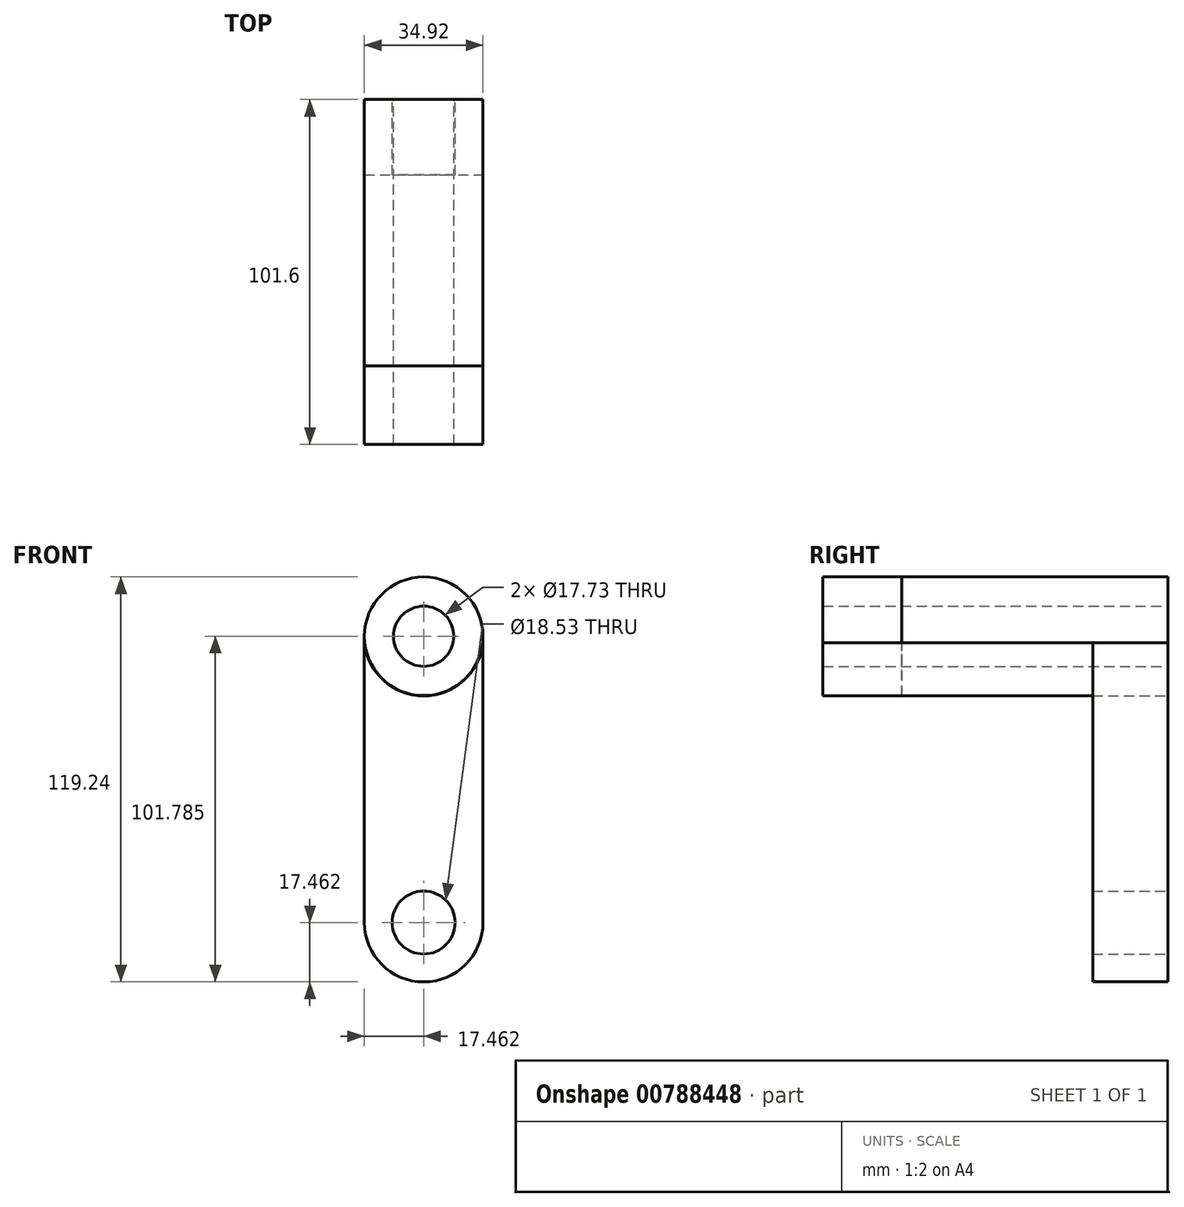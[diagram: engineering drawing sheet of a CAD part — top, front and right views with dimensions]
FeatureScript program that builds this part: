
annotation { "Feature Type Name" : "Feature", "Feature Type Description" : "" }
export const myFeature = defineFeature(function(context is Context, id is Id, definition is map)
    precondition{}
    {
        {
            var Q0;
            Q0=qCreatedBy(makeId("Front.planeOp"),FACE);
            var sketch = newSketch(context, id + "F0", { "sketchPlane" : qUnion([Q0])});
            skLineSegment(sketch, "E0.left", {"start": v(-20.9, 24.35) * mm, "end": v(-20.9, -59.97) * mm});
            skLineSegment(sketch, "E0.right", {"start": v(14, 24.35) * mm, "end": v(14, -59.97) * mm});
            skArc(sketch, "E1", {"start": v(14, 24.35) * mm, "mid": v(-3.45, 41.81) * mm, "end": v(-20.9, 24.35) * mm});
            skArc(sketch, "E2", {"start": v(-20.9, -59.97) * mm, "mid": v(-3.45, -77.43) * mm, "end": v(14, -59.97) * mm});
            skCircle(sketch, "E3", {"center": v(-3.45, 24.35) * mm, "radius": 8.86 * mm});
            skCircle(sketch, "E4", {"center": v(-3.45, -59.97) * mm, "radius": 9.27 * mm});
            skCircle(sketch, "E5", {"center": v(-3.45, 24.35) * mm, "radius": 17.57 * mm});
            skSolve(sketch);
        }
        {
            var Q0;
            Q0=makeQuery(id+"F0.imprint","IMPRINT",FACE,{"disambiguationData":[TD([[makeQuery(id+"F0.imprint","IMPRINT",EDGE,{"derivedFrom":sQuery(id+"F0.wireOp",EDGE,"E0.left")}),1.0]])]});
            extrude(context, id + "F1", {"entities" : qUnion([Q0]), "depth" : 101.6 * mm, "offsetDistance" : 25.4 * mm});
        }
        {
            var Q0;
            Q0=makeQuery(id+"F1.opExtrude","SWEPT_FACE",FACE,{"disambiguationData":[OSD([sQuery(id+"F0.wireOp",EDGE,"E0.right")])]});
            var sketch = newSketch(context, id + "F2", { "sketchPlane" : qUnion([Q0])});
            skLineSegment(sketch, "E6.top", {"start": v(-22.21, -59.97) * mm, "end": v(-78.48, -59.97) * mm});
            skLineSegment(sketch, "E6.left", {"start": v(-22.21, 24.35) * mm, "end": v(-22.21, -59.97) * mm});
            skLineSegment(sketch, "E6.right", {"start": v(-78.48, 24.35) * mm, "end": v(-78.48, -59.97) * mm});
            skLineSegment(sketch, "E7.left", {"start": v(-22.21, -59.97) * mm, "end": v(-22.21, -59.97) * mm});
            skLineSegment(sketch, "E7.right", {"start": v(-78.48, -59.97) * mm, "end": v(-78.48, -59.97) * mm});
            skLineSegment(sketch, "E8.top", {"start": v(-22.21, -99.12) * mm, "end": v(-78.48, -99.12) * mm});
            skLineSegment(sketch, "E8.left", {"start": v(-22.21, -59.97) * mm, "end": v(-22.21, -99.12) * mm});
            skLineSegment(sketch, "E8.right", {"start": v(-78.48, -59.97) * mm, "end": v(-78.48, -99.12) * mm});
            skLineSegment(sketch, "E9.bottom", {"start": v(-22.21, 24.35) * mm, "end": v(-78.48, 24.35) * mm});
            skLineSegment(sketch, "E9.top", {"start": v(-22.21, 56.67) * mm, "end": v(-78.48, 56.67) * mm});
            skLineSegment(sketch, "E9.left", {"start": v(-22.21, 24.35) * mm, "end": v(-22.21, 56.67) * mm});
            skLineSegment(sketch, "E9.right", {"start": v(-78.48, 24.35) * mm, "end": v(-78.48, 56.67) * mm});
            skSolve(sketch);
        }
        {
            var Q0;
            Q0=makeQuery(id+"F2.imprint","IMPRINT",FACE,{"disambiguationData":[TD([[makeQuery(id+"F2.imprint","IMPRINT",EDGE,{"derivedFrom":sQuery(id+"F2.wireOp",EDGE,"E6.top")}),-1.0]])]});
            var Q1;
            Q1=makeQuery(id+"F2.imprint","IMPRINT",FACE,{"disambiguationData":[TD([[makeQuery(id+"F2.imprint","IMPRINT",EDGE,{"derivedFrom":sQuery(id+"F2.wireOp",EDGE,"E6.left")}),-1.0]])]});
            var Q2;
            Q2=makeQuery(id+"F2.imprint","IMPRINT",FACE,{"disambiguationData":[TD([[makeQuery(id+"F2.imprint","IMPRINT",EDGE,{"derivedFrom":sQuery(id+"F2.wireOp",EDGE,"E9.bottom")}),1.0]])]});
            extrude(context, id + "F3", {"entities" : qUnion([Q0, Q1, Q2]), "operationType" : NewBodyOperationType.REMOVE, "oppositeDirection" : true, "depth" : 70.61 * mm, "offsetDistance" : 25.4 * mm});
        }
        {
            var Q0;
            {var subQ0=sQuery(id+"F0.wireOp",EDGE,"E1");Q0=makeQuery(id+"F0.imprint","IMPRINT",FACE,{"disambiguationData":[TD([[makeQuery(id+"F0.imprint","IMPRINT",EDGE,{"derivedFrom":subQ0}),1.0]])]});}
            extrude(context, id + "F4", {"entities" : qUnion([Q0]), "operationType" : NewBodyOperationType.REMOVE, "depth" : 71.63 * mm, "offsetDistance" : 25.4 * mm});
        }
        {
            var Q0;
            Q0=makeQuery(id+"F3.boolean.opBoolean","COPY",FACE,{"derivedFrom":makeQuery(id+"F3.opExtrude","SWEPT_FACE",FACE,{"disambiguationData":[OSD([sQuery(id+"F2.wireOp",EDGE,"E6.right"),sQuery(id+"F2.wireOp",EDGE,"E8.right"),sQuery(id+"F2.wireOp",EDGE,"E9.right")])]})});
            var sketch = newSketch(context, id + "F5", { "sketchPlane" : qUnion([Q0])});
            skCircle(sketch, "E10", {"center": v(3.45, 24.35) * mm, "radius": 17.46 * mm});
            skSolve(sketch);
        }
        {
            var Q0;
            {var subQ0=sQuery(id+"F5.wireOp",EDGE,"E10");Q0=makeQuery(id+"F5.imprint","IMPRINT",FACE,{"disambiguationData":[TD([[makeQuery(id+"F5.imprint","IMPRINT",EDGE,{"disambiguationData":[OD(0.0)],"derivedFrom":subQ0}),-1.0]])]});}
            extrude(context, id + "F6", {"entities" : qUnion([Q0]), "operationType" : NewBodyOperationType.REMOVE, "oppositeDirection" : true, "depth" : 38.35 * mm, "offsetDistance" : 25.4 * mm});
        }
        {
            var Q0;
            {var subQ0=sQuery(id+"F0.wireOp",EDGE,"E1");Q0=makeQuery(id+"F0.imprint","IMPRINT",FACE,{"disambiguationData":[TD([[makeQuery(id+"F0.imprint","IMPRINT",EDGE,{"derivedFrom":subQ0}),1.0]])]});}
            extrude(context, id + "F7", {"entities" : qUnion([Q0]), "depth" : 101.6 * mm, "offsetDistance" : 25.4 * mm});
        }
    });
